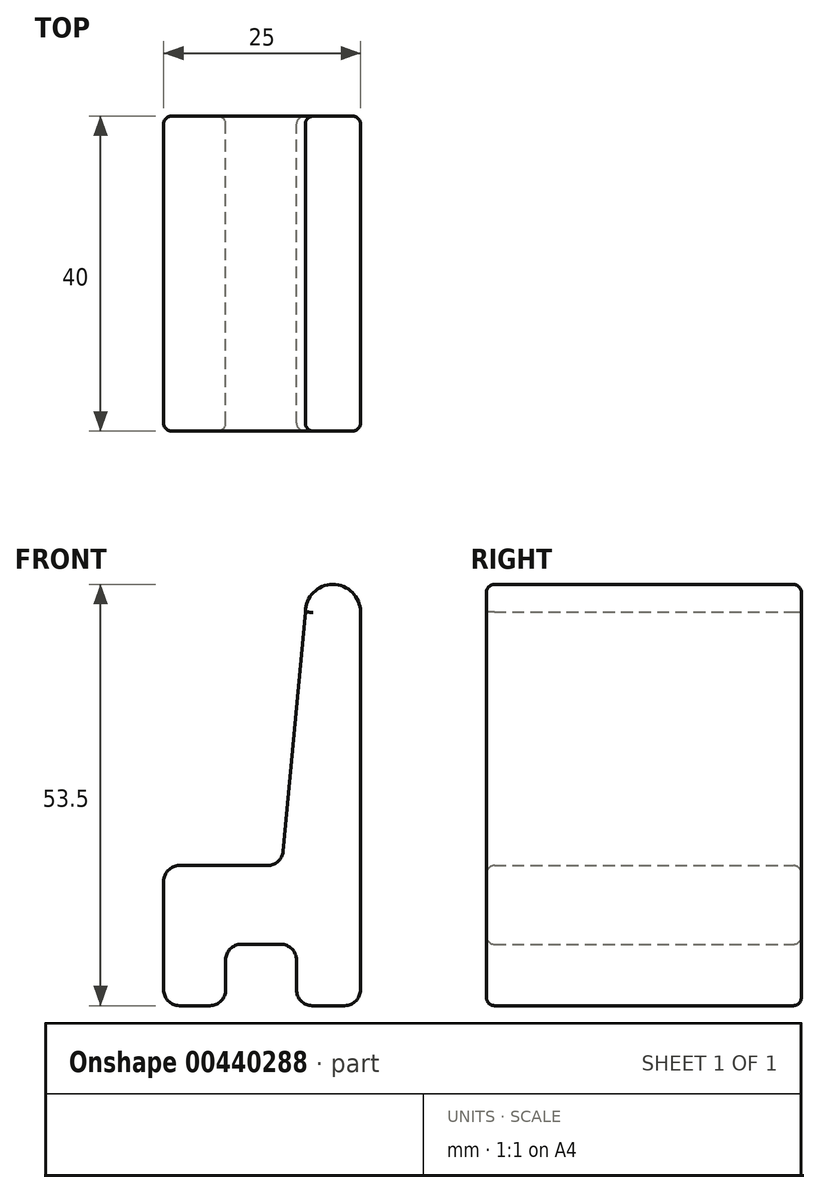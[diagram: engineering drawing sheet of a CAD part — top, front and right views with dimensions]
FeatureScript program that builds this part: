
annotation { "Feature Type Name" : "Feature", "Feature Type Description" : "" }
export const myFeature = defineFeature(function(context is Context, id is Id, definition is map)
    precondition{}
    {
        {
            var Q0;
            Q0=qCreatedBy(makeId("Front.planeOp"),FACE);
            var sketch = newSketch(context, id + "F0", { "sketchPlane" : qUnion([Q0])});
            skLineSegment(sketch, "E0.right", {"start": v(-13.44, 9.24) * mm, "end": v(-13.44, -38.76) * mm});
            skLineSegment(sketch, "E1", {"start": v(-36.44, -40.76) * mm, "end": v(-32.56, -40.76) * mm});
            skLineSegment(sketch, "E2.0", {"start": v(-21.56, -38.76) * mm, "end": v(-21.56, -34.96) * mm});
            skLineSegment(sketch, "E3.0", {"start": v(-30.56, -38.76) * mm, "end": v(-30.56, -34.96) * mm});
            skLineSegment(sketch, "E4", {"start": v(-28.56, -32.96) * mm, "end": v(-23.56, -32.96) * mm});
            skLineSegment(sketch, "E5", {"start": v(-19.56, -40.76) * mm, "end": v(-15.44, -40.76) * mm});
            skLineSegment(sketch, "E6", {"start": v(-36.44, -22.96) * mm, "end": v(-25.27, -22.96) * mm});
            skLineSegment(sketch, "E7", {"start": v(-38.44, -38.76) * mm, "end": v(-38.44, -24.96) * mm});
            skArc(sketch, "E8", {"start": v(-13.44, 9.24) * mm, "mid": v(-16.94, 12.74) * mm, "end": v(-20.44, 9.24) * mm});
            skLineSegment(sketch, "E9", {"start": v(-20.44, 9.24) * mm, "end": v(-23.27, -21.15) * mm});
            skPoint(sketch, "E10.visualSharp", {"position": v(-23.44, -22.96) * mm});
            skArc(sketch, "E10.filletArc", {"start": v(-25.27, -22.96) * mm, "mid": v(-23.92, -22.44) * mm, "end": v(-23.27, -21.15) * mm});
            skPoint(sketch, "E11.visualSharp", {"position": v(-38.44, -22.96) * mm});
            skArc(sketch, "E11.filletArc", {"start": v(-36.44, -22.96) * mm, "mid": v(-37.86, -23.55) * mm, "end": v(-38.44, -24.96) * mm});
            skPoint(sketch, "E12.visualSharp", {"position": v(-38.44, -40.76) * mm});
            skArc(sketch, "E12.filletArc", {"start": v(-38.44, -38.76) * mm, "mid": v(-37.86, -40.17) * mm, "end": v(-36.44, -40.76) * mm});
            skPoint(sketch, "E13.visualSharp", {"position": v(-30.56, -40.76) * mm});
            skArc(sketch, "E13.filletArc", {"start": v(-32.56, -40.76) * mm, "mid": v(-31.15, -40.17) * mm, "end": v(-30.56, -38.76) * mm});
            skPoint(sketch, "E14.visualSharp", {"position": v(-30.56, -32.96) * mm});
            skArc(sketch, "E14.filletArc", {"start": v(-28.56, -32.96) * mm, "mid": v(-29.98, -33.55) * mm, "end": v(-30.56, -34.96) * mm});
            skPoint(sketch, "E15.visualSharp", {"position": v(-21.56, -32.96) * mm});
            skArc(sketch, "E15.filletArc", {"start": v(-21.56, -34.96) * mm, "mid": v(-22.15, -33.55) * mm, "end": v(-23.56, -32.96) * mm});
            skPoint(sketch, "E16.visualSharp", {"position": v(-21.56, -40.76) * mm});
            skArc(sketch, "E16.filletArc", {"start": v(-21.56, -38.76) * mm, "mid": v(-20.98, -40.17) * mm, "end": v(-19.56, -40.76) * mm});
            skPoint(sketch, "E17.visualSharp", {"position": v(-13.44, -40.76) * mm});
            skArc(sketch, "E17.filletArc", {"start": v(-15.44, -40.76) * mm, "mid": v(-14.03, -40.17) * mm, "end": v(-13.44, -38.76) * mm});
            skSolve(sketch);
        }
        {
            var Q0;
            Q0=makeQuery(id+"F0.imprint","IMPRINT",FACE,{"disambiguationData":[TD([[makeQuery(id+"F0.imprint","IMPRINT",EDGE,{"derivedFrom":sQuery(id+"F0.wireOp",EDGE,"E0.right")}),-1.0]])]});
            extrude(context, id + "F1", {"entities" : qUnion([Q0]), "endBound" : BoundingType.SYMMETRIC, "depth" : 40 * mm});
        }
        {
            var Q0;
            Q0=makeQuery(id+"F1.opExtrude","CAP_FACE",FACE,{"disambiguationData":[OSD([sQuery(id+"F0.wireOp",EDGE,"E0.right"),sQuery(id+"F0.wireOp",EDGE,"E1"),sQuery(id+"F0.wireOp",EDGE,"E2.0"),sQuery(id+"F0.wireOp",EDGE,"E3.0"),sQuery(id+"F0.wireOp",EDGE,"E4"),sQuery(id+"F0.wireOp",EDGE,"E5"),sQuery(id+"F0.wireOp",EDGE,"E6"),sQuery(id+"F0.wireOp",EDGE,"E7"),sQuery(id+"F0.wireOp",EDGE,"E8"),sQuery(id+"F0.wireOp",EDGE,"E9"),sQuery(id+"F0.wireOp",EDGE,"E10.filletArc"),sQuery(id+"F0.wireOp",EDGE,"E11.filletArc"),sQuery(id+"F0.wireOp",EDGE,"E12.filletArc"),sQuery(id+"F0.wireOp",EDGE,"E13.filletArc"),sQuery(id+"F0.wireOp",EDGE,"E14.filletArc"),sQuery(id+"F0.wireOp",EDGE,"E15.filletArc"),sQuery(id+"F0.wireOp",EDGE,"E16.filletArc"),sQuery(id+"F0.wireOp",EDGE,"E17.filletArc")])],"isStart":true});
            var Q1;
            Q1=makeQuery(id+"F1.opExtrude","CAP_FACE",FACE,{"disambiguationData":[OSD([sQuery(id+"F0.wireOp",EDGE,"E0.right"),sQuery(id+"F0.wireOp",EDGE,"E1"),sQuery(id+"F0.wireOp",EDGE,"E2.0"),sQuery(id+"F0.wireOp",EDGE,"E3.0"),sQuery(id+"F0.wireOp",EDGE,"E4"),sQuery(id+"F0.wireOp",EDGE,"E5"),sQuery(id+"F0.wireOp",EDGE,"E6"),sQuery(id+"F0.wireOp",EDGE,"E7"),sQuery(id+"F0.wireOp",EDGE,"E8"),sQuery(id+"F0.wireOp",EDGE,"E9"),sQuery(id+"F0.wireOp",EDGE,"E10.filletArc"),sQuery(id+"F0.wireOp",EDGE,"E11.filletArc"),sQuery(id+"F0.wireOp",EDGE,"E12.filletArc"),sQuery(id+"F0.wireOp",EDGE,"E13.filletArc"),sQuery(id+"F0.wireOp",EDGE,"E14.filletArc"),sQuery(id+"F0.wireOp",EDGE,"E15.filletArc"),sQuery(id+"F0.wireOp",EDGE,"E16.filletArc"),sQuery(id+"F0.wireOp",EDGE,"E17.filletArc")])],"isStart":false});
            fillet(context, id + "F2", {"entities" : qUnion([Q0, Q1]), "radius" : 1 * mm, "tangentPropagation" : true, "allowEdgeOverflow" : false});
        }
    });
